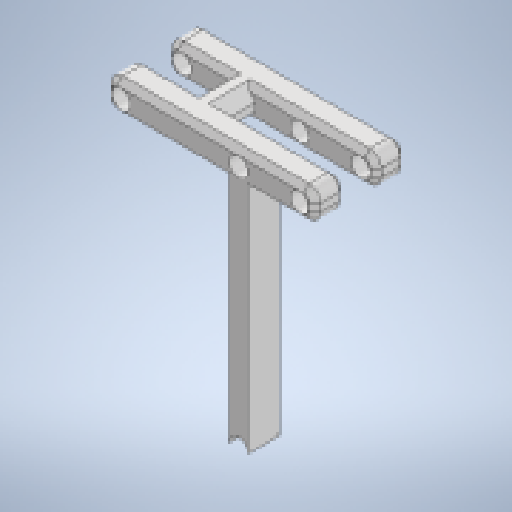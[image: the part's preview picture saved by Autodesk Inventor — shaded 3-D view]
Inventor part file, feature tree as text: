
AUTODESK INVENTOR PART (.ipt)
format: ipt  version: 2024.1 (Build 281209000, 209)  size: 286,208 bytes
history: native  units: mm
features: other x4, extrude x3, sketch x3, reference x3, projected_geometry x3, chamfer x2, fillet x1
ambient origin geometry x8: Origin, YZ Plane, XZ Plane, XY Plane, X Axis, Y Axis, Z Axis, Center Point
bodies: Body1 (feature_tree)
feature tree (19):
  other  "cross-beam"
  extrude  "Extrusion1"  Depth=55.0mm
  fillet  "Fillet1"  Radius=4.0mm
  extrude  "Extrusion2"  Depth=4.0mm
  extrude  "Extrusion3"  Depth=3.0mm
  chamfer  "Chamfer1"  Distance=5.0mm
  chamfer  "Chamfer2"  Distance=15.0mm
  sketch  "Sketch1"  dims[d0=8.0mm d2=55.0mm d4=4.0mm]
  reference  "Reference1"
  sketch  "Sketch2"  dims[d5=4.0mm d7=4.0mm]
  projected_geometry  "Projected Loop1"
  sketch  "Sketch3"  dims[d8=8.0mm d9=0.0mm d10=3.0mm d11=5.0mm d12=15.0mm d13=8.0mm d14=0.0mm d15=8.0mm d16=0.0mm d17=3.0mm d18=2.0mm d19=45.0deg d21=8.0mm d24=1.5mm d25=2.0mm d26=45.0deg]
  projected_geometry  "Projected Loop2"
  projected_geometry  "Projected Loop3"
  reference  "Reference2"
  reference  "Reference3"
  other  "<userpath>\Documents\0004-CAD\3D-cad-main\the-artifact\artifact-v2.iam"
  other  "artifact-v2.iam"
  other  "base:1"
